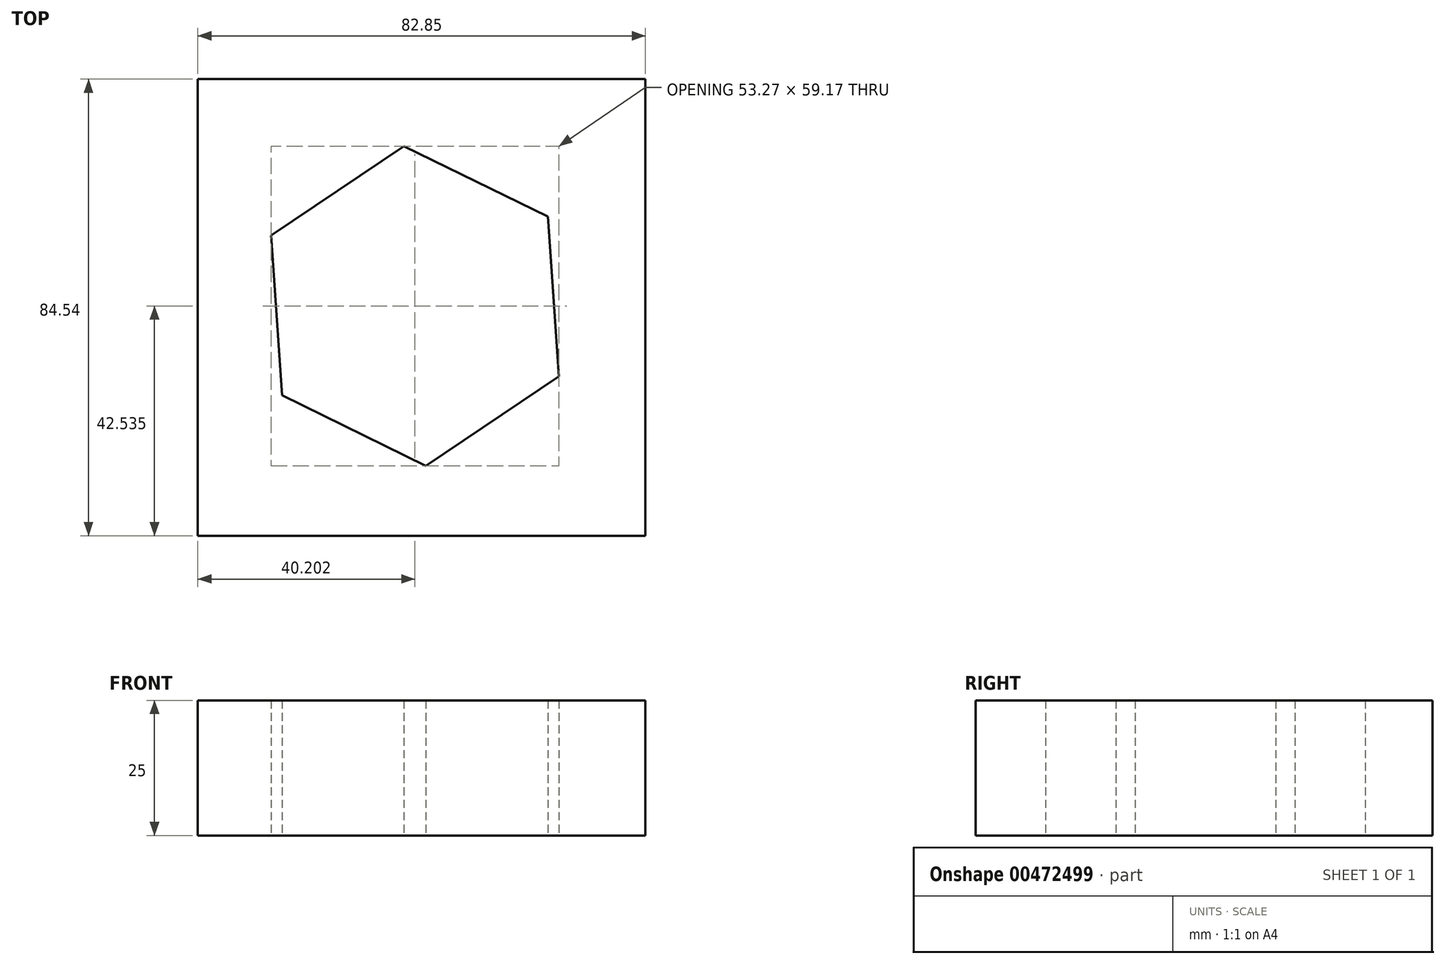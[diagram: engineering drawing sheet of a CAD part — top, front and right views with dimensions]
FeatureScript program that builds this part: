
annotation { "Feature Type Name" : "Feature", "Feature Type Description" : "" }
export const myFeature = defineFeature(function(context is Context, id is Id, definition is map)
    precondition{}
    {
        {
            var Q0;
            Q0=qCreatedBy(makeId("Top.planeOp"),FACE);
            var sketch = newSketch(context, id + "F0", { "sketchPlane" : qUnion([Q0])});
            skLineSegment(sketch, "E0.bottom", {"start": v(0, 0) * mm, "end": v(82.85, 0) * mm});
            skLineSegment(sketch, "E0.top", {"start": v(0, 84.54) * mm, "end": v(82.85, 84.54) * mm});
            skLineSegment(sketch, "E0.left", {"start": v(0, 0) * mm, "end": v(0, 84.54) * mm});
            skLineSegment(sketch, "E0.right", {"start": v(82.85, 0) * mm, "end": v(82.85, 84.54) * mm});
            skSolve(sketch);
        }
        {
            var Q0;
            Q0 = qSketchRegion(id + "F0", true);
            extrude(context, id + "F1", {"entities" : qUnion([Q0]), "depth" : 25 * mm});
        }
        {
            var Q0;
            Q0=makeQuery(id+"F1.opExtrude","CAP_FACE",FACE,{"disambiguationData":[OSD([sQuery(id+"F0.wireOp",EDGE,"E0.bottom"),sQuery(id+"F0.wireOp",EDGE,"E0.top"),sQuery(id+"F0.wireOp",EDGE,"E0.left"),sQuery(id+"F0.wireOp",EDGE,"E0.right")])],"isStart":false});
            var sketch = newSketch(context, id + "F2", { "sketchPlane" : qUnion([Q0])});
            skCircle(sketch, "E1.cCircle", {"center": v(40.2, 42.54) * mm, "radius": 29.66 * mm, "construction": true});
            skLineSegment(sketch, "E1.0", {"start": v(64.81, 59.08) * mm, "end": v(66.84, 29.5) * mm});
            skLineSegment(sketch, "E1.1", {"start": v(66.84, 29.5) * mm, "end": v(42.23, 12.95) * mm});
            skLineSegment(sketch, "E1.2", {"start": v(42.23, 12.95) * mm, "end": v(15.6, 25.99) * mm});
            skLineSegment(sketch, "E1.3", {"start": v(15.6, 25.99) * mm, "end": v(13.57, 55.57) * mm});
            skLineSegment(sketch, "E1.4", {"start": v(13.57, 55.57) * mm, "end": v(38.18, 72.12) * mm});
            skLineSegment(sketch, "E1.5", {"start": v(38.18, 72.12) * mm, "end": v(64.81, 59.08) * mm});
            skSolve(sketch);
        }
        {
            var Q0;
            Q0=makeQuery(id+"F2.imprint","IMPRINT",FACE,{"disambiguationData":[TD([[makeQuery(id+"F2.imprint","IMPRINT",EDGE,{"derivedFrom":sQuery(id+"F2.wireOp",EDGE,"E1.0")}),-1.0]])]});
            extrude(context, id + "F3", {"entities" : qUnion([Q0]), "operationType" : NewBodyOperationType.REMOVE, "depth" : 215.1 * mm, "hasDraft" : true, "draftAngle" : 3 * degree, "hasSecondDirection" : true, "secondDirectionOppositeDirection" : true, "secondDirectionDepth" : 25 * mm});
        }
    });
